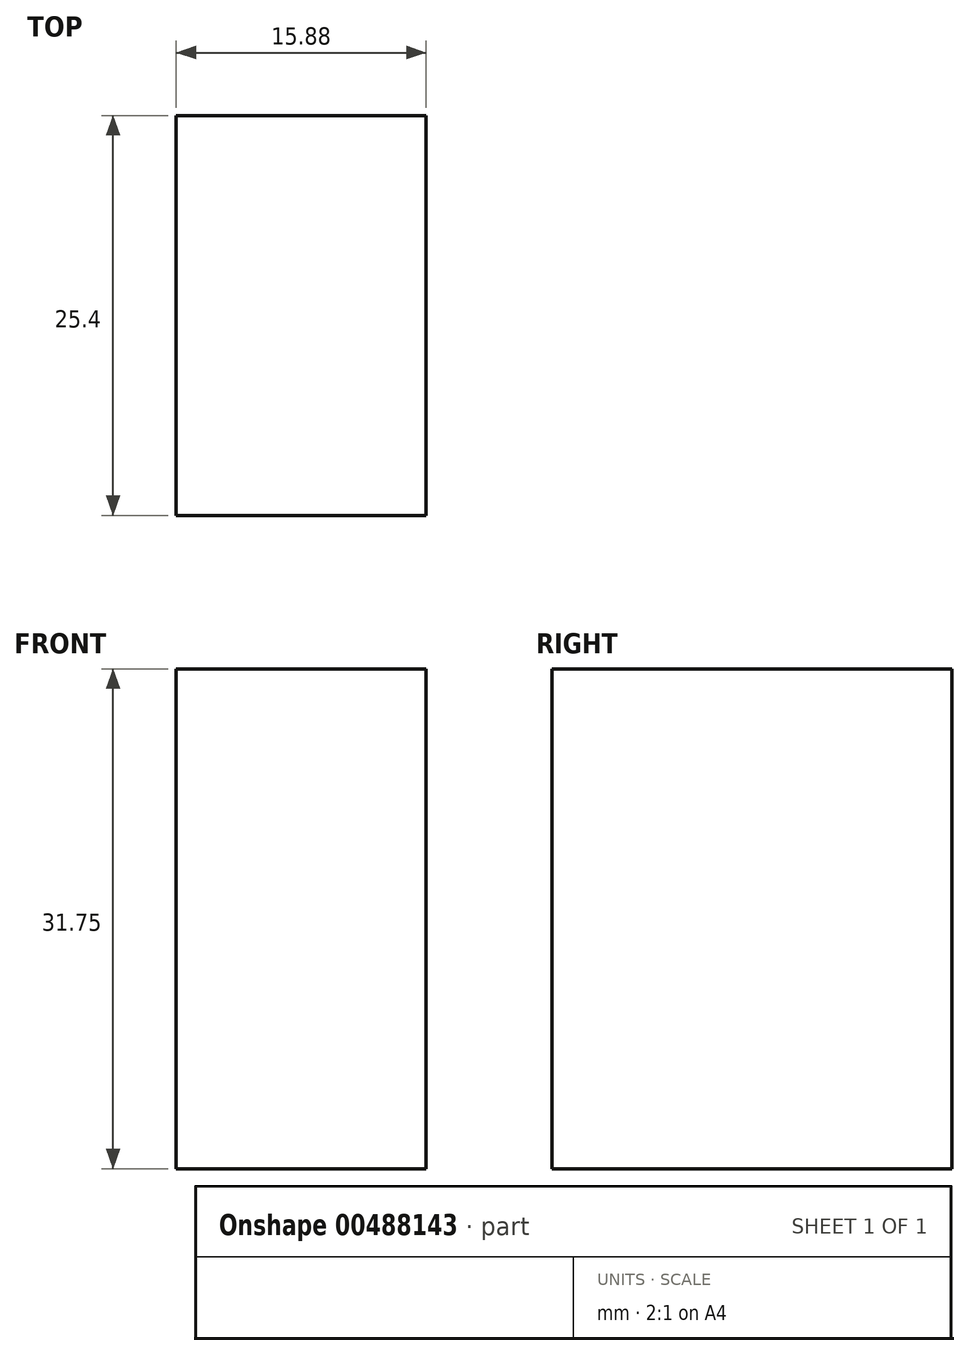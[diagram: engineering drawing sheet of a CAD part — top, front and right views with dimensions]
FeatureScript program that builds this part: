
annotation { "Feature Type Name" : "Feature", "Feature Type Description" : "" }
export const myFeature = defineFeature(function(context is Context, id is Id, definition is map)
    precondition{}
    {
        {
            var Q0;
            Q0=qCreatedBy(makeId("Front.planeOp"),FACE);
            var sketch = newSketch(context, id + "F0", { "sketchPlane" : qUnion([Q0])});
            skLineSegment(sketch, "E0", {"start": v(0, 0) * mm, "end": v(15.88, 0) * mm});
            skLineSegment(sketch, "E1", {"start": v(0, 0) * mm, "end": v(0, -31.75) * mm});
            skLineSegment(sketch, "E2", {"start": v(0, -31.75) * mm, "end": v(15.88, -31.75) * mm});
            skLineSegment(sketch, "E3", {"start": v(15.88, -31.75) * mm, "end": v(15.88, 0) * mm});
            skSolve(sketch);
        }
        {
            var Q0;
            Q0=makeQuery(id+"F0.imprint","IMPRINT",FACE,{"disambiguationData":[TD([[makeQuery(id+"F0.imprint","IMPRINT",EDGE,{"derivedFrom":sQuery(id+"F0.wireOp",EDGE,"E0")}),-1.0]])]});
            var Q1;
            Q1=makeQuery(id+"F0.imprint","IMPRINT",FACE,{"disambiguationData":[TD([[makeQuery(id+"F0.imprint","IMPRINT",EDGE,{"derivedFrom":sQuery(id+"F0.wireOp",EDGE,"E0")}),-1.0]])]});
            var Q2;
            Q2=makeQuery(id+"F0.imprint","IMPRINT",FACE,{"disambiguationData":[TD([[makeQuery(id+"F0.imprint","IMPRINT",EDGE,{"derivedFrom":sQuery(id+"F0.wireOp",EDGE,"sE00Gzr5-o4TN-UCdV-R85f-zcs0Y7AX2MqQ")}),1.0]])]});
            extrude(context, id + "F1", {"entities" : qUnion([Q0, Q1, Q2]), "depth" : 25.4 * mm, "offsetDistance" : 25.4 * mm});
        }
    });
